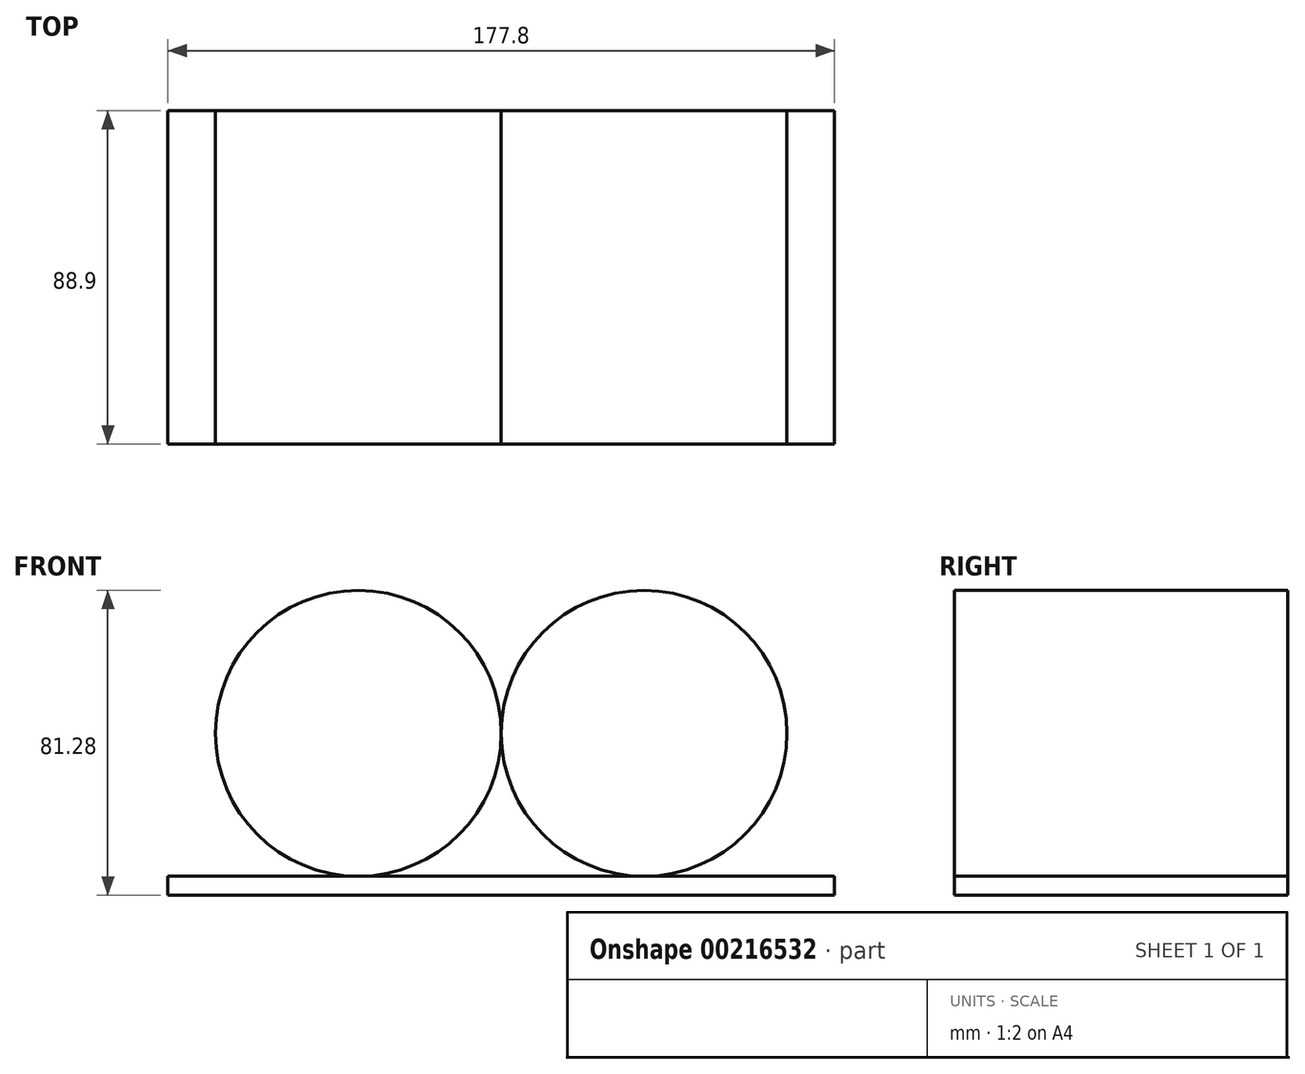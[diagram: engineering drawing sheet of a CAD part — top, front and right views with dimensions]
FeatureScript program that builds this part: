
annotation { "Feature Type Name" : "Feature", "Feature Type Description" : "" }
export const myFeature = defineFeature(function(context is Context, id is Id, definition is map)
    precondition{}
    {
        {
            var Q0;
            Q0=qCreatedBy(makeId("Front.planeOp"),FACE);
            var sketch = newSketch(context, id + "F0", { "sketchPlane" : qUnion([Q0])});
            skCircle(sketch, "E0", {"center": v(-38.1, -7.77) * mm, "radius": 38.1 * mm});
            skCircle(sketch, "E1", {"center": v(38.1, -7.77) * mm, "radius": 38.1 * mm});
            skLineSegment(sketch, "E2", {"start": v(76.2, -7.77) * mm, "end": v(-10.26, -7.77) * mm, "construction": true});
            skLineSegment(sketch, "E3.bottom", {"start": v(-88.9, -45.87) * mm, "end": v(88.9, -45.87) * mm});
            skLineSegment(sketch, "E3.top", {"start": v(-88.9, -50.95) * mm, "end": v(88.9, -50.95) * mm});
            skLineSegment(sketch, "E3.left", {"start": v(-88.9, -45.87) * mm, "end": v(-88.9, -50.95) * mm});
            skLineSegment(sketch, "E3.right", {"start": v(88.9, -45.87) * mm, "end": v(88.9, -50.95) * mm});
            skSolve(sketch);
        }
        {
            var Q0;
            {var subQ0=sQuery(id+"F0.wireOp",EDGE,"DU6uzVH8-NPqm-Om2P-tgr6-648kfvqvj1Ei");var subQ1=makeQuery(id+"F0.imprint","INTERSECT",VERTEX,{"derivedFrom":[subQ0,sQuery(id+"F0.wireOp",EDGE,"E0")]});Q0=makeQuery(id+"F0.imprint","IMPRINT",FACE,{"disambiguationData":[TD([[makeQuery(id+"F0.imprint","IMPRINT",EDGE,{"disambiguationData":[TD([[subQ1,1.0]])],"derivedFrom":subQ0}),1.0]])]});}
            var Q1;
            {var subQ0=sQuery(id+"F0.wireOp",EDGE,"699bd6fe-4fd1-4dce-9f90-8813f1e17c5f");var subQ1=makeQuery(id+"F0.imprint","INTERSECT",VERTEX,{"derivedFrom":[sQuery(id+"F0.wireOp",EDGE,"DU6uzVH8-NPqm-Om2P-tgr6-648kfvqvj1Ei"),subQ0]});Q1=makeQuery(id+"F0.imprint","IMPRINT",FACE,{"disambiguationData":[TD([[makeQuery(id+"F0.imprint","IMPRINT",EDGE,{"disambiguationData":[TD([[subQ1,-1.0]])],"derivedFrom":subQ0}),1.0]])]});}
            var Q2;
            {var subQ0=sQuery(id+"F0.wireOp",EDGE,"E1");var subQ4=makeQuery(id+"F0.imprint","INTERSECT",VERTEX,{"derivedFrom":[sQuery(id+"F0.wireOp",EDGE,"699bd6fe-4fd1-4dce-9f90-8813f1e17c5f"),subQ0]});Q2=makeQuery(id+"F0.imprint","IMPRINT",FACE,{"disambiguationData":[TD([[makeQuery(id+"F0.imprint","IMPRINT",EDGE,{"disambiguationData":[TD([[subQ4,1.0]])],"derivedFrom":subQ0}),1.0]])]});}
            var Q3;
            {var subQ0=sQuery(id+"F0.wireOp",EDGE,"01eb658d-8cb0-4c16-9e74-70905ed8b878");var subQ1=makeQuery(id+"F0.imprint","INTERSECT",VERTEX,{"derivedFrom":[sQuery(id+"F0.wireOp",EDGE,"699bd6fe-4fd1-4dce-9f90-8813f1e17c5f"),subQ0]});Q3=makeQuery(id+"F0.imprint","IMPRINT",FACE,{"disambiguationData":[TD([[makeQuery(id+"F0.imprint","IMPRINT",EDGE,{"disambiguationData":[TD([[subQ1,-1.0]])],"derivedFrom":subQ0}),1.0]])]});}
            var Q4;
            {var subQ0=sQuery(id+"F0.wireOp",EDGE,"E0");var subQ1=makeQuery(id+"F0.imprint","INTERSECT",VERTEX,{"derivedFrom":[sQuery(id+"F0.wireOp",EDGE,"DU6uzVH8-NPqm-Om2P-tgr6-648kfvqvj1Ei"),subQ0]});Q4=makeQuery(id+"F0.imprint","IMPRINT",FACE,{"disambiguationData":[TD([[makeQuery(id+"F0.imprint","IMPRINT",EDGE,{"disambiguationData":[TD([[subQ1,1.0]])],"derivedFrom":subQ0}),1.0]])]});}
            var Q5;
            Q5=makeQuery(id+"F0.imprint","IMPRINT",FACE,{"disambiguationData":[TD([[makeQuery(id+"F0.imprint","IMPRINT",EDGE,{"derivedFrom":sQuery(id+"F0.wireOp",EDGE,"E3.top")}),1.0]])]});
            var Q6;
            Q6=sQuery(id+"F0.wireOp",EDGE,"DU6uzVH8-NPqm-Om2P-tgr6-648kfvqvj1Ei");
            var Q7;
            Q7=sQuery(id+"F0.wireOp",EDGE,"699bd6fe-4fd1-4dce-9f90-8813f1e17c5f");
            var Q8;
            Q8=sQuery(id+"F0.wireOp",EDGE,"E0");
            var Q9;
            Q9=sQuery(id+"F0.wireOp",EDGE,"E1");
            var Q10;
            Q10=sQuery(id+"F0.wireOp",EDGE,"01eb658d-8cb0-4c16-9e74-70905ed8b878");
            var Q11;
            Q11=sQuery(id+"F0.wireOp",EDGE,"E3.bottom");
            var Q12;
            Q12=sQuery(id+"F0.wireOp",EDGE,"E3.top");
            var Q13;
            Q13=sQuery(id+"F0.wireOp",EDGE,"E3.left");
            var Q14;
            Q14=sQuery(id+"F0.wireOp",EDGE,"E3.right");
            extrude(context, id + "F1", {"entities" : qUnion([Q0, Q1, Q2, Q3, Q4, Q5]), "surfaceEntities" : qUnion([Q6, Q7, Q8, Q9, Q10, Q11, Q12, Q13, Q14]), "depth" : 88.9 * mm});
        }
    });
